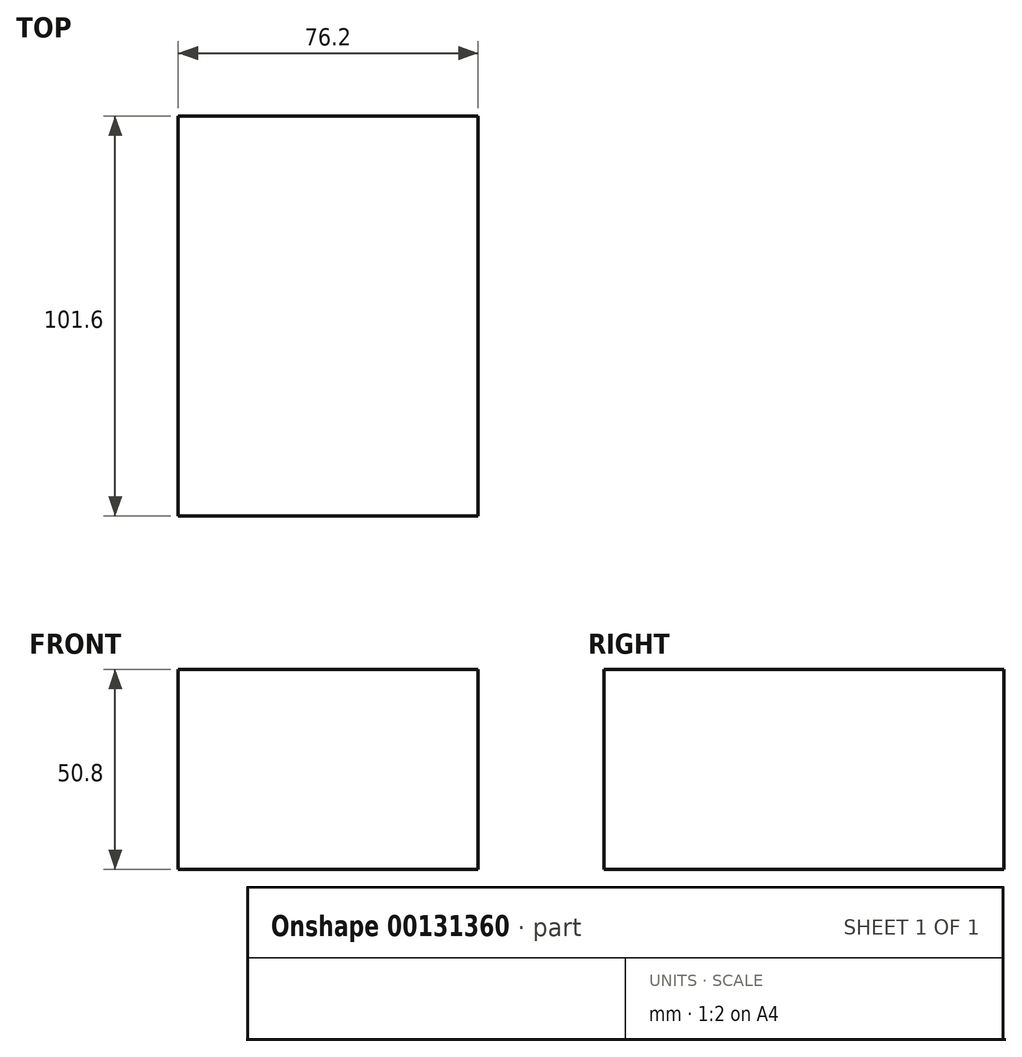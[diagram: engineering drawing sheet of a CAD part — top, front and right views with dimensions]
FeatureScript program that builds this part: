
annotation { "Feature Type Name" : "Feature", "Feature Type Description" : "" }
export const myFeature = defineFeature(function(context is Context, id is Id, definition is map)
    precondition{}
    {
        {
            var Q0;
            Q0=qCreatedBy(makeId("Front.planeOp"),FACE);
            var sketch = newSketch(context, id + "F0", { "sketchPlane" : qUnion([Q0])});
            skLineSegment(sketch, "E0.bottom", {"start": v(-38.1, 25.4) * mm, "end": v(38.1, 25.4) * mm});
            skLineSegment(sketch, "E0.top", {"start": v(-38.1, -25.4) * mm, "end": v(38.1, -25.4) * mm});
            skLineSegment(sketch, "E0.left", {"start": v(-38.1, 25.4) * mm, "end": v(-38.1, -25.4) * mm});
            skLineSegment(sketch, "E0.right", {"start": v(38.1, 25.4) * mm, "end": v(38.1, -25.4) * mm});
            skPoint(sketch, "E0.middle", {"position": v(0, 0) * mm});
            skSolve(sketch);
        }
        {
            var Q0;
            Q0 = qSketchRegion(id + "F0", true);
            extrude(context, id + "F1", {"entities" : qUnion([Q0]), "depth" : 101.6 * mm});
        }
    });
